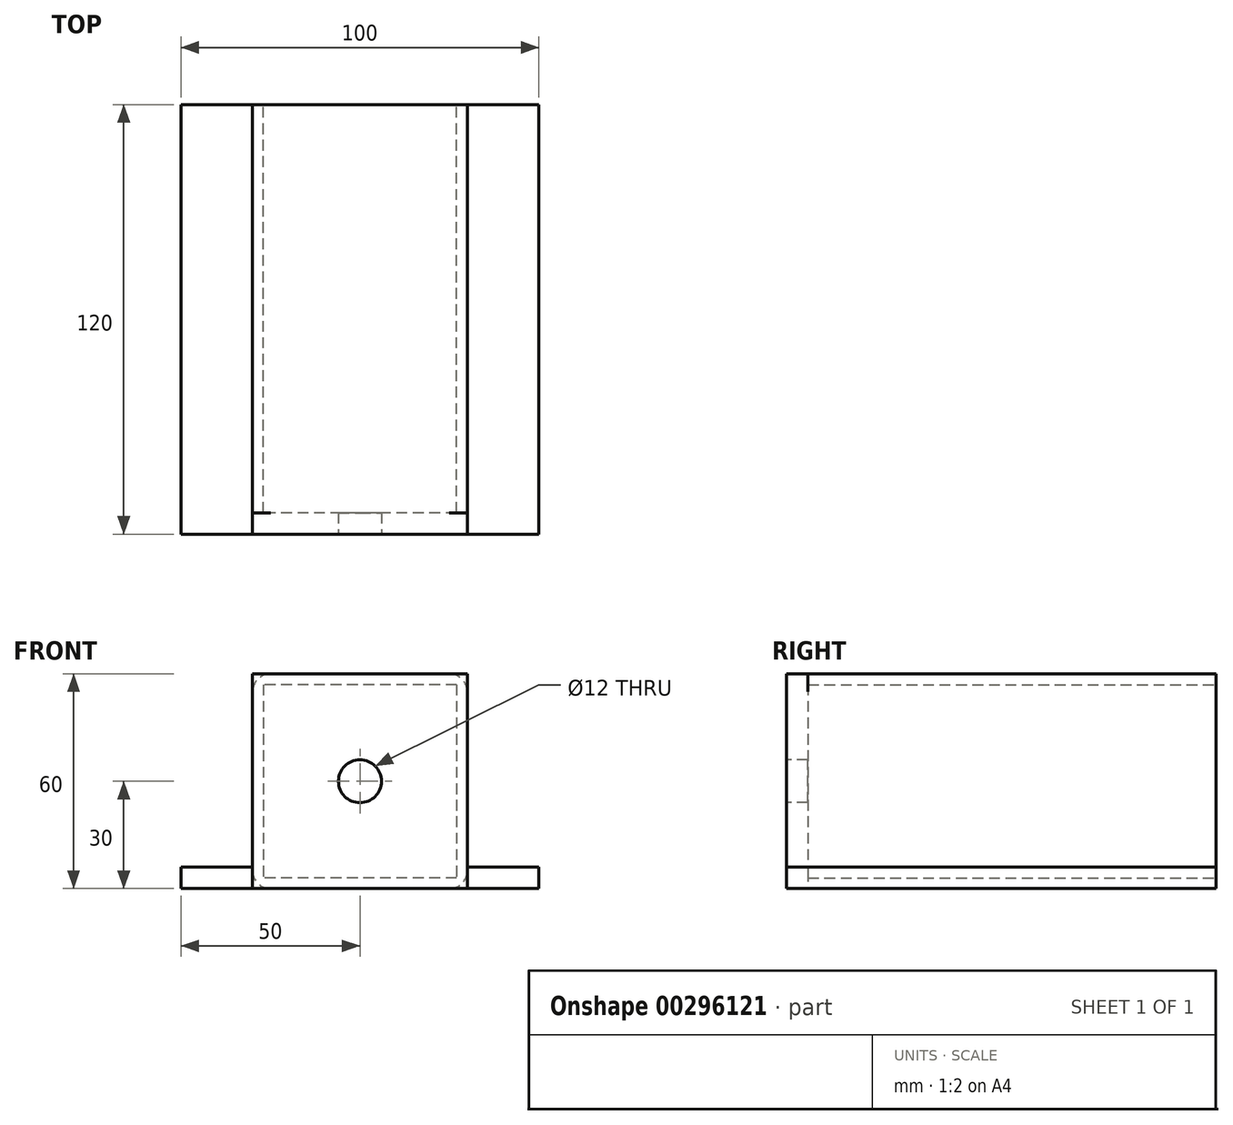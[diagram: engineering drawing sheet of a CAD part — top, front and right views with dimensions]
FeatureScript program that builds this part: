
annotation { "Feature Type Name" : "Feature", "Feature Type Description" : "" }
export const myFeature = defineFeature(function(context is Context, id is Id, definition is map)
    precondition{}
    {
        {
            var Q0;
            Q0=qCreatedBy(makeId("Front.planeOp"),FACE);
            var sketch = newSketch(context, id + "F0", { "sketchPlane" : qUnion([Q0])});
            skLineSegment(sketch, "E0.bottom", {"start": v(25, 30) * mm, "end": v(-25, 30) * mm});
            skLineSegment(sketch, "E0.top", {"start": v(25, -30) * mm, "end": v(-25, -30) * mm});
            skLineSegment(sketch, "E0.left", {"start": v(30, 25) * mm, "end": v(30, -25) * mm});
            skLineSegment(sketch, "E0.right", {"start": v(-30, 25) * mm, "end": v(-30, -25) * mm});
            skPoint(sketch, "E0.middle", {"position": v(0, 0) * mm});
            skPoint(sketch, "E1.visualSharp", {"position": v(-30, 30) * mm});
            skArc(sketch, "E1.filletArc", {"start": v(-25, 30) * mm, "mid": v(-28.54, 28.54) * mm, "end": v(-30, 25) * mm});
            skPoint(sketch, "E2.visualSharp", {"position": v(30, 30) * mm});
            skArc(sketch, "E2.filletArc", {"start": v(30, 25) * mm, "mid": v(28.54, 28.54) * mm, "end": v(25, 30) * mm});
            skPoint(sketch, "E3.visualSharp", {"position": v(30, -30) * mm});
            skArc(sketch, "E3.filletArc", {"start": v(25, -30) * mm, "mid": v(28.54, -28.54) * mm, "end": v(30, -25) * mm});
            skPoint(sketch, "E4.visualSharp", {"position": v(-30, -30) * mm});
            skArc(sketch, "E4.filletArc", {"start": v(-30, -25) * mm, "mid": v(-28.54, -28.54) * mm, "end": v(-25, -30) * mm});
            skLineSegment(sketch, "E5.0", {"start": v(-27, 27) * mm, "end": v(-27, -27) * mm});
            skLineSegment(sketch, "E5.1", {"start": v(27, 27) * mm, "end": v(-27, 27) * mm});
            skLineSegment(sketch, "E5.2", {"start": v(27, 27) * mm, "end": v(27, -27) * mm});
            skLineSegment(sketch, "E5.3", {"start": v(27, -27) * mm, "end": v(-27, -27) * mm});
            skSolve(sketch);
        }
        {
            var Q0;
            Q0=makeQuery(id+"F0.imprint","IMPRINT",FACE,{"disambiguationData":[TD([[makeQuery(id+"F0.imprint","IMPRINT",EDGE,{"derivedFrom":sQuery(id+"F0.wireOp",EDGE,"E0.bottom")}),1.0]])]});
            extrude(context, id + "F1", {"entities" : qUnion([Q0]), "depth" : 120 * mm});
        }
        {
            var Q0;
            Q0=makeQuery(id+"F1.opExtrude","CAP_FACE",FACE,{"disambiguationData":[OSD([sQuery(id+"F0.wireOp",EDGE,"E0.bottom"),sQuery(id+"F0.wireOp",EDGE,"E0.top"),sQuery(id+"F0.wireOp",EDGE,"E0.left"),sQuery(id+"F0.wireOp",EDGE,"E0.right"),sQuery(id+"F0.wireOp",EDGE,"E1.filletArc"),sQuery(id+"F0.wireOp",EDGE,"E2.filletArc"),sQuery(id+"F0.wireOp",EDGE,"E3.filletArc"),sQuery(id+"F0.wireOp",EDGE,"E4.filletArc"),sQuery(id+"F0.wireOp",EDGE,"E5.0"),sQuery(id+"F0.wireOp",EDGE,"E5.1"),sQuery(id+"F0.wireOp",EDGE,"E5.2"),sQuery(id+"F0.wireOp",EDGE,"E5.3")])],"isStart":false});
            var sketch = newSketch(context, id + "F2", { "sketchPlane" : qUnion([Q0])});
            skLineSegment(sketch, "E6.bottom", {"start": v(-30, 30) * mm, "end": v(30, 30) * mm});
            skLineSegment(sketch, "E6.top", {"start": v(-30, -30) * mm, "end": v(30, -30) * mm});
            skLineSegment(sketch, "E6.left", {"start": v(-30, 30) * mm, "end": v(-30, -30) * mm});
            skLineSegment(sketch, "E6.right", {"start": v(30, 30) * mm, "end": v(30, -30) * mm});
            skPoint(sketch, "E6.middle", {"position": v(0, 0) * mm});
            skCircle(sketch, "E7", {"center": v(0, 0) * mm, "radius": 6 * mm});
            skSolve(sketch);
        }
        {
            var Q0;
            Q0 = qSketchRegion(id + "F2", true);
            extrude(context, id + "F3", {"entities" : qUnion([Q0]), "operationType" : NewBodyOperationType.ADD, "oppositeDirection" : true, "depth" : 6 * mm});
        }
        {
            var Q0;
            Q0=makeQuery(id+"F3.boolean.opBoolean","MERGE",FACE,{"derivedFrom":[makeQuery(id+"F1.opExtrude","SWEPT_FACE",FACE,{"disambiguationData":[OSD([sQuery(id+"F0.wireOp",EDGE,"E0.top")])]}),makeQuery(id+"F3.opExtrude","SWEPT_FACE",FACE,{"disambiguationData":[OSD([sQuery(id+"F2.wireOp",EDGE,"E6.top")])]})]});
            var sketch = newSketch(context, id + "F4", { "sketchPlane" : qUnion([Q0])});
            skLineSegment(sketch, "E8.bottom", {"start": v(30, 120) * mm, "end": v(50, 120) * mm});
            skLineSegment(sketch, "E8.top", {"start": v(30, 0) * mm, "end": v(50, 0) * mm});
            skLineSegment(sketch, "E8.left", {"start": v(30, 120) * mm, "end": v(30, 0) * mm});
            skLineSegment(sketch, "E8.right", {"start": v(50, 120) * mm, "end": v(50, 0) * mm});
            skLineSegment(sketch, "E9.bottom", {"start": v(-30, 120) * mm, "end": v(-50, 120) * mm});
            skLineSegment(sketch, "E9.top", {"start": v(-30, 0) * mm, "end": v(-50, 0) * mm});
            skLineSegment(sketch, "E9.left", {"start": v(-30, 120) * mm, "end": v(-30, 0) * mm});
            skLineSegment(sketch, "E9.right", {"start": v(-50, 120) * mm, "end": v(-50, 0) * mm});
            skSolve(sketch);
        }
        {
            var Q0;
            Q0 = qSketchRegion(id + "F4", true);
            extrude(context, id + "F5", {"entities" : qUnion([Q0]), "oppositeDirection" : true, "depth" : 6 * mm});
        }
    });
